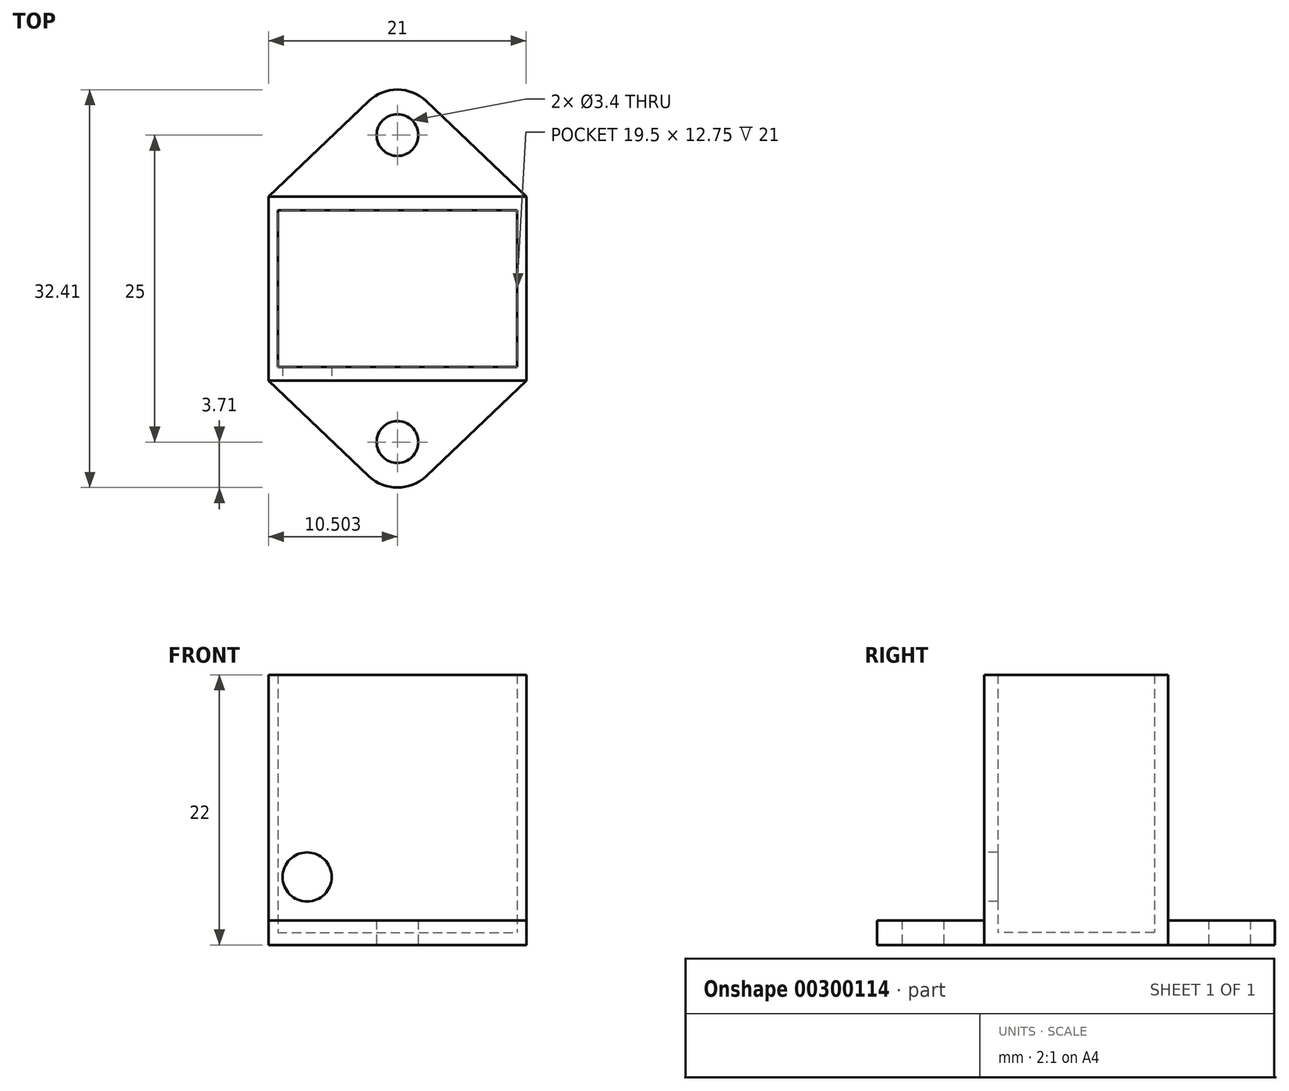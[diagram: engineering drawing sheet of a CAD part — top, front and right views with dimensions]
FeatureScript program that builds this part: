
annotation { "Feature Type Name" : "Feature", "Feature Type Description" : "" }
export const myFeature = defineFeature(function(context is Context, id is Id, definition is map)
    precondition{}
    {
        {
            var Q0;
            Q0=qCreatedBy(makeId("Top.planeOp"),FACE);
            var sketch = newSketch(context, id + "F0", { "sketchPlane" : qUnion([Q0])});
            skLineSegment(sketch, "E0.bottom", {"start": v(21.8, -3.09) * mm, "end": v(41.3, -3.09) * mm});
            skLineSegment(sketch, "E0.top", {"start": v(21.8, -15.84) * mm, "end": v(41.3, -15.84) * mm});
            skLineSegment(sketch, "E0.left", {"start": v(21.8, -3.09) * mm, "end": v(21.8, -15.84) * mm});
            skLineSegment(sketch, "E0.right", {"start": v(41.3, -3.09) * mm, "end": v(41.3, -15.84) * mm});
            skLineSegment(sketch, "E1.bottom", {"start": v(21.05, -1.96) * mm, "end": v(42.05, -1.96) * mm});
            skLineSegment(sketch, "E1.top", {"start": v(21.05, -16.96) * mm, "end": v(42.05, -16.96) * mm});
            skLineSegment(sketch, "E1.left", {"start": v(21.05, -1.96) * mm, "end": v(21.05, -16.96) * mm});
            skLineSegment(sketch, "E1.right", {"start": v(42.05, -1.96) * mm, "end": v(42.05, -16.96) * mm});
            skLineSegment(sketch, "E2", {"start": v(42.05, -9.46) * mm, "end": v(21.05, -9.46) * mm, "construction": true});
            skLineSegment(sketch, "E3", {"start": v(31.55, -1.96) * mm, "end": v(31.55, -16.96) * mm, "construction": true});
            skLineSegment(sketch, "E4", {"start": v(41.3, -9.46) * mm, "end": v(21.8, -9.46) * mm, "construction": true});
            skLineSegment(sketch, "E5", {"start": v(31.55, -3.09) * mm, "end": v(31.55, -15.84) * mm, "construction": true});
            skLineSegment(sketch, "E6", {"start": v(31.55, -1.96) * mm, "end": v(31.55, 8.04) * mm, "construction": true});
            skLineSegment(sketch, "E7", {"start": v(31.55, -16.96) * mm, "end": v(31.55, -26.96) * mm, "construction": true});
            skLineSegment(sketch, "E8", {"start": v(31.55, -26.96) * mm, "end": v(42.05, -16.96) * mm});
            skLineSegment(sketch, "E9", {"start": v(31.55, -26.96) * mm, "end": v(21.05, -16.96) * mm});
            skLineSegment(sketch, "E10", {"start": v(21.05, -1.96) * mm, "end": v(31.55, 8.04) * mm});
            skLineSegment(sketch, "E11", {"start": v(31.55, 8.04) * mm, "end": v(42.05, -1.96) * mm});
            skCircle(sketch, "E12", {"center": v(31.55, 3.04) * mm, "radius": 1.7 * mm});
            skCircle(sketch, "E13", {"center": v(31.55, -21.96) * mm, "radius": 1.7 * mm});
            skSolve(sketch);
        }
        {
            var Q0;
            Q0=makeQuery(id+"F0.imprint","IMPRINT",FACE,{"disambiguationData":[TD([[makeQuery(id+"F0.imprint","IMPRINT",EDGE,{"derivedFrom":sQuery(id+"F0.wireOp",EDGE,"E0.bottom")}),1.0]])]});
            extrude(context, id + "F1", {"entities" : qUnion([Q0]), "depth" : 22 * mm});
        }
        {
            var Q0;
            Q0=makeQuery(id+"F0.imprint","IMPRINT",FACE,{"disambiguationData":[TD([[makeQuery(id+"F0.imprint","IMPRINT",EDGE,{"derivedFrom":sQuery(id+"F0.wireOp",EDGE,"E0.bottom")}),-1.0]])]});
            extrude(context, id + "F2", {"entities" : qUnion([Q0]), "operationType" : NewBodyOperationType.ADD, "depth" : 1 * mm});
        }
        {
            var Q0;
            Q0=makeQuery(id+"F0.imprint","IMPRINT",FACE,{"disambiguationData":[TD([[makeQuery(id+"F0.imprint","IMPRINT",EDGE,{"derivedFrom":sQuery(id+"F0.wireOp",EDGE,"E1.bottom")}),1.0]])]});
            var Q1;
            Q1=makeQuery(id+"F0.imprint","IMPRINT",FACE,{"disambiguationData":[TD([[makeQuery(id+"F0.imprint","IMPRINT",EDGE,{"derivedFrom":sQuery(id+"F0.wireOp",EDGE,"E1.top")}),-1.0]])]});
            extrude(context, id + "F3", {"entities" : qUnion([Q0, Q1]), "operationType" : NewBodyOperationType.ADD, "depth" : 2 * mm});
        }
        {
            var Q0;
            Q0=makeQuery(id+"F3.opExtrude","SWEPT_EDGE",EDGE,{"disambiguationData":[OSD([sQuery(id+"F0.wireOp",EDGE,"E10"),sQuery(id+"F0.wireOp",EDGE,"E11")])]});
            var Q1;
            Q1=makeQuery(id+"F3.opExtrude","SWEPT_EDGE",EDGE,{"disambiguationData":[OSD([sQuery(id+"F0.wireOp",EDGE,"E8"),sQuery(id+"F0.wireOp",EDGE,"E9")])]});
            fillet(context, id + "F4", {"entities" : qUnion([Q0, Q1]), "radius" : 3.4 * mm, "tangentPropagation" : true, "allowEdgeOverflow" : false});
        }
        {
            var Q0;
            Q0=makeQuery(id+"F1.opExtrude","SWEPT_FACE",FACE,{"disambiguationData":[OSD([sQuery(id+"F0.wireOp",EDGE,"E1.top")])]});
            var sketch = newSketch(context, id + "F5", { "sketchPlane" : qUnion([Q0])});
            skCircle(sketch, "E14", {"center": v(24.2, 5.53) * mm, "radius": 2 * mm});
            skSolve(sketch);
        }
        {
            var Q0;
            Q0=makeQuery(id+"F5.imprint","IMPRINT",FACE,{"disambiguationData":[TD([[makeQuery(id+"F5.imprint","IMPRINT",EDGE,{"derivedFrom":sQuery(id+"F5.wireOp",EDGE,"E14")}),1.0]])]});
            extrude(context, id + "F6", {"entities" : qUnion([Q0]), "operationType" : NewBodyOperationType.REMOVE, "oppositeDirection" : true, "depth" : 2.5 * mm});
        }
    });
